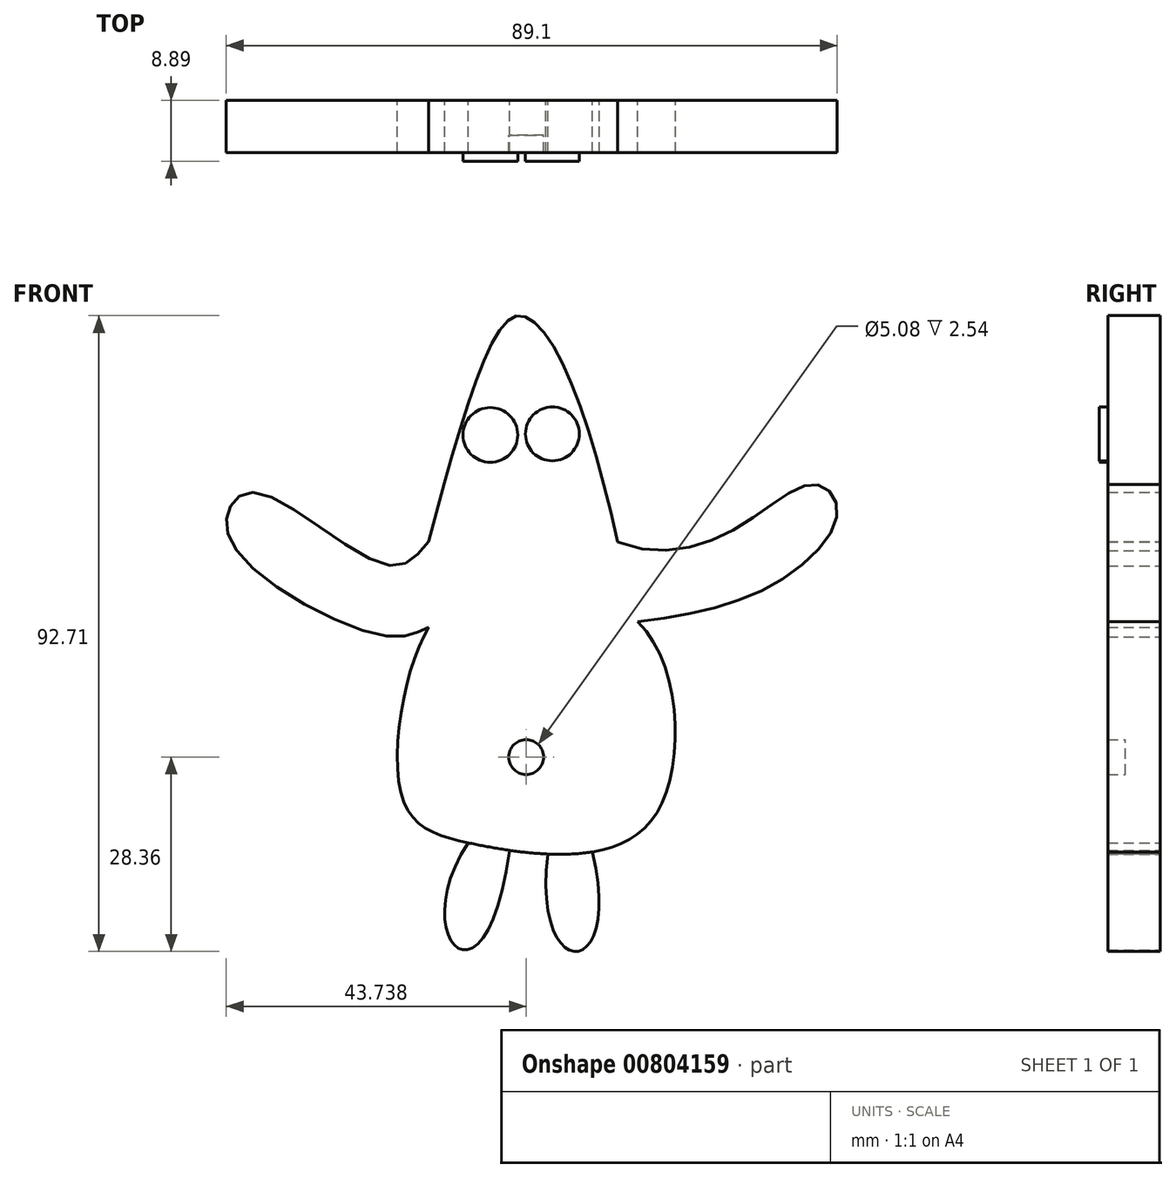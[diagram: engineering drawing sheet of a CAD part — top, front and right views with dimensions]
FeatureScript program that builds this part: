
annotation { "Feature Type Name" : "Feature", "Feature Type Description" : "" }
export const myFeature = defineFeature(function(context is Context, id is Id, definition is map)
    precondition{}
    {
        {
            var Q0;
            Q0=qCreatedBy(makeId("Front.planeOp"),FACE);
            var sketch = newSketch(context, id + "F0", { "sketchPlane" : qUnion([Q0])});
            skFitSpline(sketch, "E0", {"points": [v(-9, 31.4) * mm, v(0, 59.87) * mm, v(4.25, 64.35) * mm, v(9.54, 59.26) * mm, v(18.53, 31.36) * mm], "startDerivative": vector(26.49, 99.05) * mm, "endDerivative": vector(21.14, -98.33) * mm});
            skFitSpline(sketch, "E1", {"points": [v(-9, 31.4) * mm, v(-14.87, 27.94) * mm, v(-33.4, 38.4) * mm, v(-38.03, 36.3) * mm, v(-36.43, 29.36) * mm, v(-14.67, 17.56) * mm, v(-9, 18.89) * mm], "startDerivative": vector(-35.8, -43.68) * mm, "endDerivative": vector(35.39, 11.68) * mm});
            skFitSpline(sketch, "E2", {"points": [v(21.49, 19.72) * mm, v(42.08, 25.64) * mm, v(50.58, 35.8) * mm, v(47.37, 39.74) * mm, v(36.39, 33.63) * mm, v(18.53, 31.36) * mm], "startDerivative": vector(90.19, 10.88) * mm, "endDerivative": vector(-83.5, 33.14) * mm});
            skFitSpline(sketch, "E3", {"points": [v(-9, 18.89) * mm, v(-12.75, -6.23) * mm, v(-3.2, -12.51) * mm, v(14.84, -13.83) * mm, v(25.47, -5.68) * mm, v(21.49, 19.72) * mm], "startDerivative": vector(-43.67, -68.7) * mm, "endDerivative": vector(-74.37, 70.8) * mm});
            skFitSpline(sketch, "E4", {"points": [v(-3.2, -12.51) * mm, v(2.79, -13.6) * mm], "startDerivative": vector(-27.8, -40.35) * mm, "endDerivative": vector(10.26, 76.54) * mm});
            skFitSpline(sketch, "E5", {"points": [v(8.37, -14.15) * mm, v(14.84, -13.83) * mm], "startDerivative": vector(-7.01, -57.88) * mm, "endDerivative": vector(-14.35, 57.03) * mm});
            skCircle(sketch, "E6", {"center": v(0, 46.97) * mm, "radius": 4 * mm});
            skCircle(sketch, "E7", {"center": v(9.04, 47.1) * mm, "radius": 3.93 * mm});
            skFitSpline(sketch, "E8", {"points": [v(-4.1, 38.45) * mm, v(-0.95, 33.44) * mm, v(8.04, 33.17) * mm, v(13.13, 38.08) * mm], "startDerivative": vector(6.6, -19.48) * mm, "endDerivative": vector(12.31, 17.8) * mm});
            skCircle(sketch, "E9", {"center": v(5.22, 0) * mm, "radius": 2.54 * mm});
            skSolve(sketch);
        }
        {
            var Q0;
            {var subQ0=sQuery(id+"F0.wireOp",EDGE,"E5");Q0=makeQuery(id+"F0.imprint","IMPRINT",FACE,{"disambiguationData":[TD([[makeQuery(id+"F0.imprint","IMPRINT",EDGE,{"derivedFrom":subQ0}),1.0]])]});}
            var Q1;
            {var subQ0=sQuery(id+"F0.wireOp",EDGE,"E4");Q1=makeQuery(id+"F0.imprint","IMPRINT",FACE,{"disambiguationData":[TD([[makeQuery(id+"F0.imprint","IMPRINT",EDGE,{"derivedFrom":subQ0}),1.0]])]});}
            extrude(context, id + "F1", {"entities" : qUnion([Q0, Q1]), "depth" : 7.62 * mm, "offsetDistance" : 25.4 * mm});
        }
        {
            var Q0;
            Q0=makeQuery(id+"F0.imprint","IMPRINT",FACE,{"disambiguationData":[TD([[makeQuery(id+"F0.imprint","IMPRINT",EDGE,{"derivedFrom":sQuery(id+"F0.wireOp",EDGE,"E0")}),-1.0]])]});
            extrude(context, id + "F2", {"entities" : qUnion([Q0]), "depth" : 7.62 * mm, "offsetDistance" : 25.4 * mm});
        }
        {
            var Q0;
            Q0=makeQuery(id+"F0.imprint","IMPRINT",FACE,{"disambiguationData":[TD([[makeQuery(id+"F0.imprint","IMPRINT",EDGE,{"derivedFrom":sQuery(id+"F0.wireOp",EDGE,"E9")}),1.0]])]});
            extrude(context, id + "F3", {"entities" : qUnion([Q0]), "operationType" : NewBodyOperationType.ADD, "depth" : 5.08 * mm, "offsetDistance" : 25.4 * mm});
        }
        {
            var Q0;
            Q0=makeQuery(id+"F0.imprint","IMPRINT",FACE,{"disambiguationData":[TD([[makeQuery(id+"F0.imprint","IMPRINT",EDGE,{"derivedFrom":sQuery(id+"F0.wireOp",EDGE,"E6")}),1.0]])]});
            var Q1;
            Q1=makeQuery(id+"F0.imprint","IMPRINT",FACE,{"disambiguationData":[TD([[makeQuery(id+"F0.imprint","IMPRINT",EDGE,{"derivedFrom":sQuery(id+"F0.wireOp",EDGE,"E7")}),1.0]])]});
            extrude(context, id + "F4", {"entities" : qUnion([Q0, Q1]), "operationType" : NewBodyOperationType.ADD, "depth" : 8.9 * mm, "offsetDistance" : 25.4 * mm});
        }
        {
            var Q0;
            Q0=sQuery(id+"F0.wireOp",EDGE,"E8");
            extrude(context, id + "F5", {"bodyType" : ToolBodyType.SURFACE, "surfaceEntities" : qUnion([Q0]), "depth" : 8.9 * mm, "offsetDistance" : 25.4 * mm});
        }
    });
